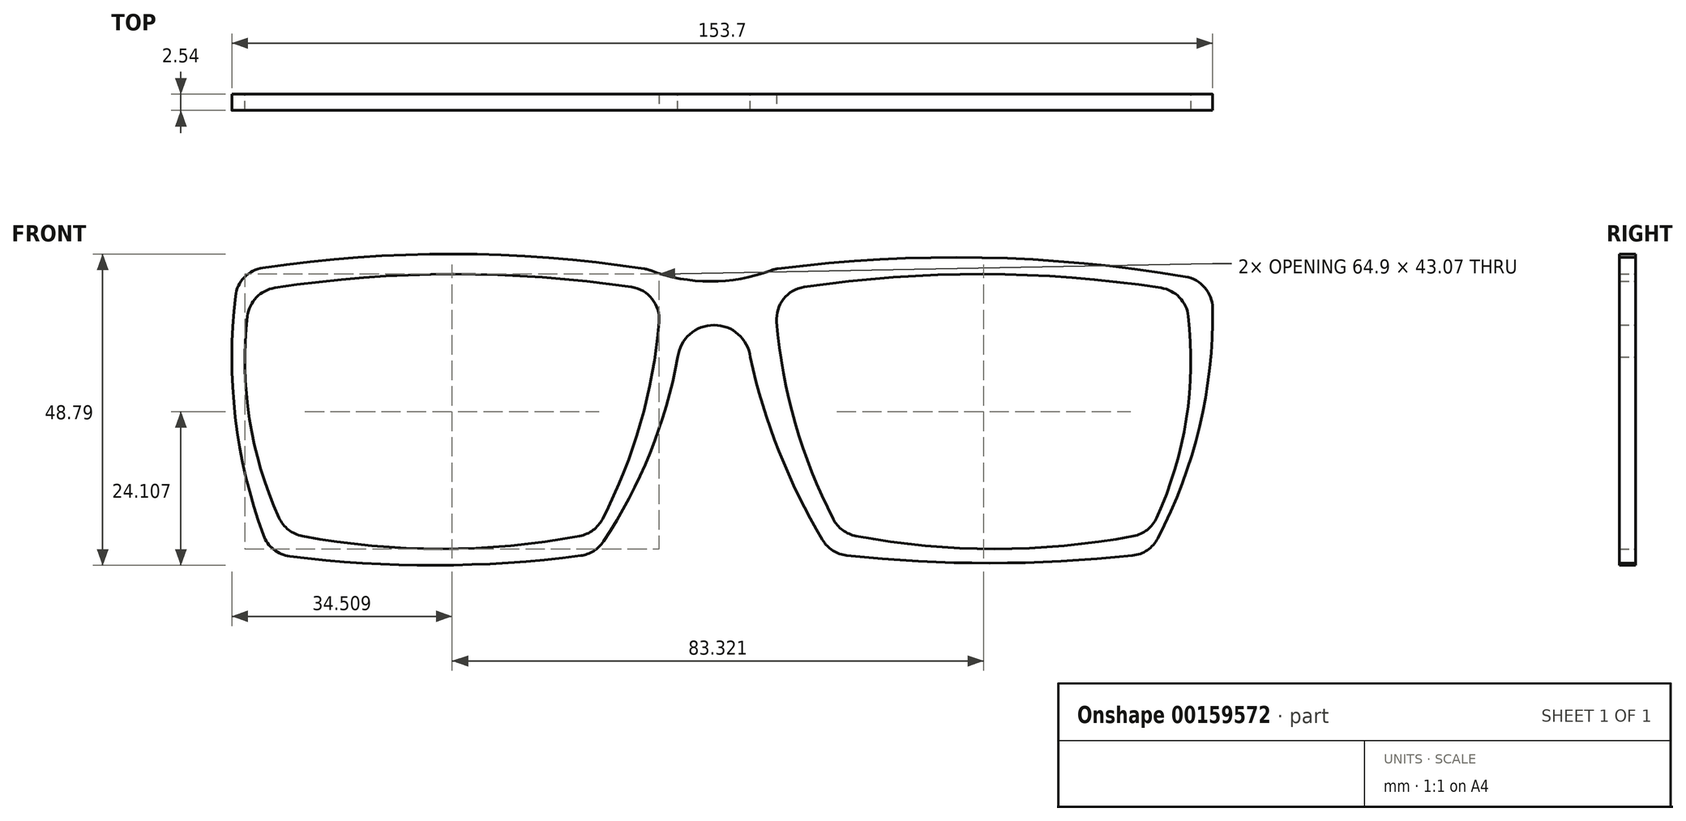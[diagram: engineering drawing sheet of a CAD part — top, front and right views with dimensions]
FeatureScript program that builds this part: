
annotation { "Feature Type Name" : "Feature", "Feature Type Description" : "" }
export const myFeature = defineFeature(function(context is Context, id is Id, definition is map)
    precondition{}
    {
        {
            var Q0;
            Q0=qCreatedBy(makeId("Front.planeOp"),FACE);
            var sketch = newSketch(context, id + "F0", { "sketchPlane" : qUnion([Q0])});
            skArc(sketch, "E0", {"start": v(-8.95, 0) * mm, "mid": v(-41.05, 2.76) * mm, "end": v(-73.15, 0) * mm});
            skArc(sketch, "E1", {"start": v(-19.24, -37.81) * mm, "mid": v(-11.82, -19.53) * mm, "end": v(-8.95, 0) * mm});
            skArc(sketch, "E2", {"start": v(-67.63, -37.81) * mm, "mid": v(-43.43, -40.3) * mm, "end": v(-19.24, -37.81) * mm});
            skArc(sketch, "E3", {"start": v(-73.15, 0) * mm, "mid": v(-73.5, -19.36) * mm, "end": v(-67.63, -37.81) * mm});
            skArc(sketch, "E4.MirrorCS", {"start": v(8.95, 0) * mm, "mid": v(41.05, 2.76) * mm, "end": v(73.15, 0) * mm});
            skArc(sketch, "E5.MirrorCS", {"start": v(67.63, -37.81) * mm, "mid": v(43.43, -40.3) * mm, "end": v(19.24, -37.81) * mm});
            skArc(sketch, "E6.MirrorCS", {"start": v(73.15, 0) * mm, "mid": v(73.5, -19.36) * mm, "end": v(67.63, -37.81) * mm});
            skArc(sketch, "E7.MirrorCS", {"start": v(19.24, -37.81) * mm, "mid": v(11.82, -19.53) * mm, "end": v(8.95, 0) * mm});
            skArc(sketch, "E8", {"start": v(-11.05, 3.52) * mm, "mid": v(-43.07, 5.9) * mm, "end": v(-75.06, 3.14) * mm});
            skArc(sketch, "E9", {"start": v(-11.05, 3.52) * mm, "mid": v(-1.14, 1.62) * mm, "end": v(8.76, 3.52) * mm});
            skArc(sketch, "E10", {"start": v(77.34, 1.62) * mm, "mid": v(43.13, 5.3) * mm, "end": v(8.76, 3.52) * mm});
            skPoint(sketch, "E10.startSnap0", {"position": v(-1.14, 1.62) * mm});
            skArc(sketch, "E11", {"start": v(-75.06, 3.14) * mm, "mid": v(-75.66, -19.3) * mm, "end": v(-70.1, -41.05) * mm});
            skArc(sketch, "E12", {"start": v(-70.1, -41.05) * mm, "mid": v(-44.67, -42.88) * mm, "end": v(-19.24, -41.05) * mm});
            skArc(sketch, "E13", {"start": v(-19.24, -41.05) * mm, "mid": v(-11.07, -26.36) * mm, "end": v(-6.29, -10.25) * mm});
            skArc(sketch, "E14", {"start": v(5.08, -10.25) * mm, "mid": v(-0.6, -5.22) * mm, "end": v(-6.29, -10.25) * mm});
            skArc(sketch, "E15", {"start": v(5.08, -10.25) * mm, "mid": v(10.05, -26.2) * mm, "end": v(17.72, -41.05) * mm});
            skArc(sketch, "E16", {"start": v(17.72, -41.05) * mm, "mid": v(42.67, -42.54) * mm, "end": v(67.63, -41.05) * mm});
            skArc(sketch, "E17", {"start": v(67.63, -41.05) * mm, "mid": v(75.65, -20.44) * mm, "end": v(77.34, 1.62) * mm});
            skSolve(sketch);
        }
        {
            var Q0;
            Q0=makeQuery(id+"F0.imprint","IMPRINT",FACE,{"disambiguationData":[TD([[makeQuery(id+"F0.imprint","IMPRINT",EDGE,{"derivedFrom":sQuery(id+"F0.wireOp",EDGE,"E0")}),-1.0]])]});
            extrude(context, id + "F1", {"entities" : qUnion([Q0]), "depth" : 2.54 * mm});
        }
        {
            var Q0;
            Q0=makeQuery(id+"F1.opExtrude","SWEPT_EDGE",EDGE,{"disambiguationData":[OSD([sQuery(id+"F0.wireOp",EDGE,"E8"),sQuery(id+"F0.wireOp",EDGE,"E11")])]});
            var Q1;
            Q1=makeQuery(id+"F1.opExtrude","SWEPT_EDGE",EDGE,{"disambiguationData":[OSD([sQuery(id+"F0.wireOp",EDGE,"E11"),sQuery(id+"F0.wireOp",EDGE,"E12")])]});
            var Q2;
            Q2=makeQuery(id+"F1.opExtrude","SWEPT_EDGE",EDGE,{"disambiguationData":[OSD([sQuery(id+"F0.wireOp",EDGE,"E12"),sQuery(id+"F0.wireOp",EDGE,"E13")])]});
            var Q3;
            Q3=makeQuery(id+"F1.opExtrude","SWEPT_EDGE",EDGE,{"disambiguationData":[OSD([sQuery(id+"F0.wireOp",EDGE,"E15"),sQuery(id+"F0.wireOp",EDGE,"E16")])]});
            var Q4;
            Q4=makeQuery(id+"F1.opExtrude","SWEPT_EDGE",EDGE,{"disambiguationData":[OSD([sQuery(id+"F0.wireOp",EDGE,"E16"),sQuery(id+"F0.wireOp",EDGE,"E17")])]});
            var Q5;
            Q5=makeQuery(id+"F1.opExtrude","SWEPT_EDGE",EDGE,{"disambiguationData":[OSD([sQuery(id+"F0.wireOp",EDGE,"E10"),sQuery(id+"F0.wireOp",EDGE,"E17")])]});
            var Q6;
            Q6=makeQuery(id+"F1.opExtrude","SWEPT_EDGE",EDGE,{"disambiguationData":[OSD([sQuery(id+"F0.wireOp",EDGE,"E8"),sQuery(id+"F0.wireOp",EDGE,"E9")])]});
            var Q7;
            Q7=makeQuery(id+"F1.opExtrude","SWEPT_EDGE",EDGE,{"disambiguationData":[OSD([sQuery(id+"F0.wireOp",EDGE,"E9"),sQuery(id+"F0.wireOp",EDGE,"E10")])]});
            fillet(context, id + "F2", {"entities" : qUnion([Q0, Q1, Q2, Q3, Q4, Q5, Q6, Q7]), "radius" : 5.08 * mm, "tangentPropagation" : true, "allowEdgeOverflow" : false});
        }
        {
            var Q0;
            Q0=makeQuery(id+"F1.opExtrude","SWEPT_EDGE",EDGE,{"disambiguationData":[OSD([sQuery(id+"F0.wireOp",EDGE,"E0"),sQuery(id+"F0.wireOp",EDGE,"E3")])]});
            var Q1;
            Q1=makeQuery(id+"F1.opExtrude","SWEPT_EDGE",EDGE,{"disambiguationData":[OSD([sQuery(id+"F0.wireOp",EDGE,"E2"),sQuery(id+"F0.wireOp",EDGE,"E3")])]});
            var Q2;
            Q2=makeQuery(id+"F1.opExtrude","SWEPT_EDGE",EDGE,{"disambiguationData":[OSD([sQuery(id+"F0.wireOp",EDGE,"E1"),sQuery(id+"F0.wireOp",EDGE,"E2")])]});
            var Q3;
            Q3=makeQuery(id+"F1.opExtrude","SWEPT_EDGE",EDGE,{"disambiguationData":[OSD([sQuery(id+"F0.wireOp",EDGE,"E0"),sQuery(id+"F0.wireOp",EDGE,"E1")])]});
            var Q4;
            Q4=makeQuery(id+"F1.opExtrude","SWEPT_EDGE",EDGE,{"disambiguationData":[OSD([sQuery(id+"F0.wireOp",EDGE,"E4.MirrorCS"),sQuery(id+"F0.wireOp",EDGE,"E6.MirrorCS")])]});
            var Q5;
            Q5=makeQuery(id+"F1.opExtrude","SWEPT_EDGE",EDGE,{"disambiguationData":[OSD([sQuery(id+"F0.wireOp",EDGE,"E5.MirrorCS"),sQuery(id+"F0.wireOp",EDGE,"E6.MirrorCS")])]});
            var Q6;
            Q6=makeQuery(id+"F1.opExtrude","SWEPT_EDGE",EDGE,{"disambiguationData":[OSD([sQuery(id+"F0.wireOp",EDGE,"E5.MirrorCS"),sQuery(id+"F0.wireOp",EDGE,"E7.MirrorCS")])]});
            var Q7;
            Q7=makeQuery(id+"F1.opExtrude","SWEPT_EDGE",EDGE,{"disambiguationData":[OSD([sQuery(id+"F0.wireOp",EDGE,"E4.MirrorCS"),sQuery(id+"F0.wireOp",EDGE,"E7.MirrorCS")])]});
            fillet(context, id + "F3", {"entities" : qUnion([Q0, Q1, Q2, Q3, Q4, Q5, Q6, Q7]), "radius" : 5.08 * mm, "tangentPropagation" : true, "allowEdgeOverflow" : false});
        }
    });
